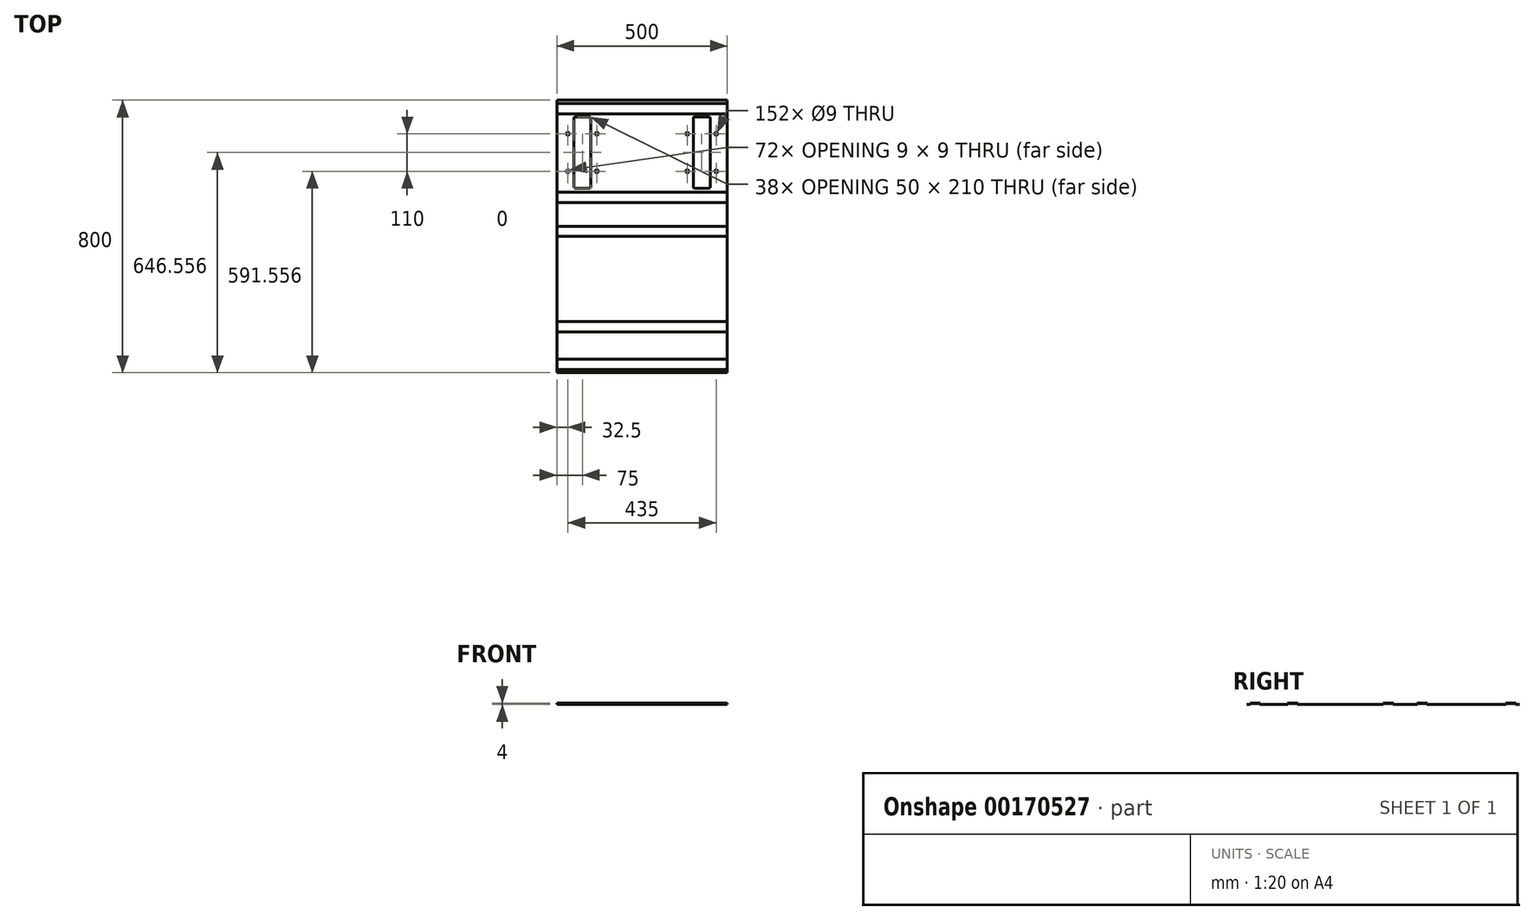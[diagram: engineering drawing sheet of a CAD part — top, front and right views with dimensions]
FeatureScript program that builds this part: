
annotation { "Feature Type Name" : "Feature", "Feature Type Description" : "" }
export const myFeature = defineFeature(function(context is Context, id is Id, definition is map)
    precondition{}
    {
        {
            var Q0;
            Q0=qCreatedBy(makeId("Right.planeOp"),FACE);
            var sketch = newSketch(context, id + "F0", { "sketchPlane" : qUnion([Q0])});
            skLineSegment(sketch, "E0.bottom", {"start": v(-25.28, 0) * mm, "end": v(-14.28, 0) * mm});
            skLineSegment(sketch, "E0.top", {"start": v(-25.28, 1) * mm, "end": v(-15.28, 1) * mm});
            skLineSegment(sketch, "E0.left", {"start": v(-25.28, 0) * mm, "end": v(-25.28, 1) * mm});
            skLineSegment(sketch, "E0.right", {"start": v(774.72, 0) * mm, "end": v(774.72, 1) * mm});
            skLineSegment(sketch, "E1.0", {"start": v(-14.28, 3) * mm, "end": v(13.72, 3) * mm});
            skLineSegment(sketch, "E2.0", {"start": v(-15.28, 4) * mm, "end": v(14.72, 4) * mm});
            skLineSegment(sketch, "E3", {"start": v(764.72, 4) * mm, "end": v(764.72, 1) * mm});
            skLineSegment(sketch, "E4", {"start": v(734.72, 4) * mm, "end": v(734.72, 1) * mm});
            skPoint(sketch, "E5.orphan", {"position": v(734.72, 10.86) * mm});
            skPoint(sketch, "E6.orphan", {"position": v(764.72, 9.78) * mm});
            skLineSegment(sketch, "E7.0", {"start": v(763.72, 3) * mm, "end": v(763.72, 1) * mm});
            skLineSegment(sketch, "E8.0", {"start": v(735.72, 3) * mm, "end": v(735.72, 1) * mm});
            skLineSegment(sketch, "E9.trimOffspring", {"start": v(764.72, 1) * mm, "end": v(774.72, 1) * mm});
            skLineSegment(sketch, "E10", {"start": v(763.72, 1) * mm, "end": v(763.72, 0) * mm});
            skLineSegment(sketch, "E11", {"start": v(735.72, 1) * mm, "end": v(735.72, 0) * mm});
            skLineSegment(sketch, "E12.trimOffspring", {"start": v(735.72, 3) * mm, "end": v(763.72, 3) * mm});
            skLineSegment(sketch, "E13.trimOffspring", {"start": v(763.72, 0) * mm, "end": v(774.72, 0) * mm});
            skLineSegment(sketch, "E14", {"start": v(504.72, 4) * mm, "end": v(504.72, 1) * mm});
            skLineSegment(sketch, "E15", {"start": v(474.72, 4) * mm, "end": v(474.72, 1) * mm});
            skLineSegment(sketch, "E16.trimOffspring", {"start": v(503.72, 0) * mm, "end": v(735.72, 0) * mm});
            skLineSegment(sketch, "E17.trimOffspring", {"start": v(504.72, 1) * mm, "end": v(734.72, 1) * mm});
            skLineSegment(sketch, "E18.trimOffspring", {"start": v(475.72, 3) * mm, "end": v(475.72, 0) * mm});
            skLineSegment(sketch, "E19.trimOffspring", {"start": v(503.72, 3) * mm, "end": v(503.72, 0) * mm});
            skLineSegment(sketch, "E20.trimOffspring", {"start": v(475.72, 3) * mm, "end": v(503.72, 3) * mm});
            skPoint(sketch, "E21.orphan", {"position": v(474.72, 0) * mm});
            skLineSegment(sketch, "E22.trimOffspring", {"start": v(734.72, 4) * mm, "end": v(764.72, 4) * mm});
            skLineSegment(sketch, "E23", {"start": v(-15.28, 4) * mm, "end": v(-15.28, 1) * mm});
            skLineSegment(sketch, "E24", {"start": v(14.72, 4) * mm, "end": v(14.72, 1) * mm});
            skLineSegment(sketch, "E25", {"start": v(94.72, 4) * mm, "end": v(94.72, 1) * mm});
            skLineSegment(sketch, "E26", {"start": v(124.72, 4) * mm, "end": v(124.72, 1) * mm});
            skPoint(sketch, "E27.orphan", {"position": v(-15.28, 10.77) * mm});
            skLineSegment(sketch, "E28.0", {"start": v(-14.28, 3) * mm, "end": v(-14.28, 0) * mm});
            skLineSegment(sketch, "E29.0", {"start": v(95.72, 4) * mm, "end": v(95.72, 0) * mm});
            skLineSegment(sketch, "E30.0", {"start": v(123.72, 3) * mm, "end": v(123.72, 0) * mm});
            skPoint(sketch, "E31.orphan", {"position": v(124.72, 12.9) * mm});
            skPoint(sketch, "E32.orphan", {"position": v(94.72, 12.13) * mm});
            skLineSegment(sketch, "E33.trimOffspring", {"start": v(14.72, 1) * mm, "end": v(94.72, 1) * mm});
            skPoint(sketch, "E34.orphan", {"position": v(-15.28, 0) * mm});
            skLineSegment(sketch, "E35.trimOffspring", {"start": v(13.72, 0) * mm, "end": v(95.72, 0) * mm});
            skLineSegment(sketch, "E36.trimOffspring", {"start": v(94.72, 3) * mm, "end": v(123.72, 3) * mm});
            skLineSegment(sketch, "E37.trimOffspring", {"start": v(13.72, 3) * mm, "end": v(13.72, 0) * mm});
            skPoint(sketch, "E38.orphan", {"position": v(14.72, 11.16) * mm});
            skLineSegment(sketch, "E39.trimOffspring", {"start": v(94.72, 4) * mm, "end": v(124.72, 4) * mm});
            skPoint(sketch, "E40.orphan", {"position": v(14.72, 0) * mm});
            skLineSegment(sketch, "E41.trimOffspring", {"start": v(124.72, 1) * mm, "end": v(374.72, 1) * mm});
            skLineSegment(sketch, "E42.trimOffspring", {"start": v(123.72, 0) * mm, "end": v(375.72, 0) * mm});
            skPoint(sketch, "E43.orphan", {"position": v(94.72, 0) * mm});
            skPoint(sketch, "E44.orphan", {"position": v(124.72, 0) * mm});
            skLineSegment(sketch, "E45.trimOffspring", {"start": v(375.72, 3) * mm, "end": v(404.01, 3) * mm});
            skLineSegment(sketch, "E46", {"start": v(374.72, 4) * mm, "end": v(374.72, 1) * mm});
            skLineSegment(sketch, "E47", {"start": v(405, 4) * mm, "end": v(405.03, 1) * mm});
            skLineSegment(sketch, "E48.trimOffspring", {"start": v(374.72, 4) * mm, "end": v(405, 4) * mm});
            skLineSegment(sketch, "E49.trimOffspring", {"start": v(474.72, 4) * mm, "end": v(504.72, 4) * mm});
            skLineSegment(sketch, "E50.0", {"start": v(404.01, 3) * mm, "end": v(404.05, -0.01) * mm});
            skLineSegment(sketch, "E51.trimOffspring", {"start": v(405.03, 1) * mm, "end": v(474.72, 1) * mm});
            skLineSegment(sketch, "E52.trimOffspring", {"start": v(404.05, 0) * mm, "end": v(475.72, 0) * mm});
            skLineSegment(sketch, "E53.trimOffspring", {"start": v(375.72, 3) * mm, "end": v(375.72, 0) * mm});
            skPoint(sketch, "E54.orphan", {"position": v(374.72, 0) * mm});
            skPoint(sketch, "E55.orphan", {"position": v(374.72, 30.11) * mm});
            skPoint(sketch, "E56.orphan", {"position": v(404.72, 31.49) * mm});
            skSolve(sketch);
        }
        {
            var Q0;
            {var subQ3=sQuery(id+"F0.wireOp",EDGE,"E2.0");Q0=makeQuery(id+"F0.imprint","IMPRINT",FACE,{"disambiguationData":[TD([[makeQuery(id+"F0.imprint","IMPRINT",EDGE,{"derivedFrom":subQ3}),-1.0]])]});}
            var Q1;
            Q1=makeQuery(id+"F0.imprint","IMPRINT",FACE,{"disambiguationData":[TD([[makeQuery(id+"F0.imprint","IMPRINT",EDGE,{"derivedFrom":sQuery(id+"F0.wireOp",EDGE,"E0.right")}),1.0]])]});
            var Q2;
            {var subQ0=sQuery(id+"F0.wireOp",EDGE,"E35.trimOffspring");Q2=makeQuery(id+"F0.imprint","IMPRINT",FACE,{"disambiguationData":[TD([[makeQuery(id+"F0.imprint","IMPRINT",EDGE,{"derivedFrom":subQ0}),1.0]])]});}
            var Q3;
            {var subQ0=sQuery(id+"F0.wireOp",EDGE,"E37.trimOffspring");var subQ1=sQuery(id+"F0.wireOp",EDGE,"E1.0");var subQ2=makeQuery(id+"F0.imprint","INTERSECT",VERTEX,{"derivedFrom":[subQ1,subQ0]});Q3=makeQuery(id+"F0.imprint","IMPRINT",FACE,{"disambiguationData":[TD([[makeQuery(id+"F0.imprint","IMPRINT",EDGE,{"disambiguationData":[TD([[subQ2,1.0]])],"derivedFrom":subQ1}),-1.0]])]});}
            var Q4;
            {var subQ0=sQuery(id+"F0.wireOp",EDGE,"E39.trimOffspring");var subQ1=sQuery(id+"F0.wireOp",EDGE,"E25");var subQ2=makeQuery(id+"F0.imprint","INTERSECT",VERTEX,{"derivedFrom":[subQ1,subQ0]});Q4=makeQuery(id+"F0.imprint","IMPRINT",FACE,{"disambiguationData":[TD([[makeQuery(id+"F0.imprint","IMPRINT",EDGE,{"disambiguationData":[TD([[subQ2,-1.0]])],"derivedFrom":subQ1}),1.0]])]});}
            var Q5;
            Q5=makeQuery(id+"F0.imprint","IMPRINT",FACE,{"disambiguationData":[TD([[makeQuery(id+"F0.imprint","IMPRINT",EDGE,{"derivedFrom":sQuery(id+"F0.wireOp",EDGE,"E0.bottom")}),1.0]])]});
            extrude(context, id + "F1", {"entities" : qUnion([Q0, Q1, Q2, Q3, Q4, Q5]), "oppositeDirection" : true, "depth" : 500 * mm});
        }
        {
            var Q0;
            Q0=makeQuery(id+"F1.opExtrude","SWEPT_FACE",FACE,{"disambiguationData":[OSD([sQuery(id+"F0.wireOp",EDGE,"E17.trimOffspring")])]});
            var sketch = newSketch(context, id + "F2", { "sketchPlane" : qUnion([Q0])});
            skLineSegment(sketch, "E57", {"start": v(-250, 774.7) * mm, "end": v(-250, 270.25) * mm, "construction": true});
            skLineSegment(sketch, "E58", {"start": v(0.24, 551.28) * mm, "end": v(-799.76, 551.28) * mm, "construction": true});
            skLineSegment(sketch, "E59.bottom", {"start": v(-445, 726.28) * mm, "end": v(-405, 726.28) * mm});
            skLineSegment(sketch, "E59.top", {"start": v(-445, 516.28) * mm, "end": v(-405, 516.28) * mm});
            skLineSegment(sketch, "E59.left", {"start": v(-450, 721.28) * mm, "end": v(-450, 521.28) * mm});
            skLineSegment(sketch, "E59.right", {"start": v(-400, 721.28) * mm, "end": v(-400, 521.28) * mm});
            skCircle(sketch, "E60", {"center": v(-467.5, 676.28) * mm, "radius": 4.5 * mm});
            skLineSegment(sketch, "E61", {"start": v(-450, 621.28) * mm, "end": v(-872.27, 621.28) * mm, "construction": true});
            skLineSegment(sketch, "E62", {"start": v(-425, 726.28) * mm, "end": v(-425, 666.8) * mm, "construction": true});
            skCircle(sketch, "E63.MirrorC", {"center": v(-467.5, 566.28) * mm, "radius": 4.5 * mm});
            skCircle(sketch, "E64.MirrorC", {"center": v(-382.5, 676.28) * mm, "radius": 4.5 * mm});
            skCircle(sketch, "E65.MirrorC", {"center": v(-382.5, 566.28) * mm, "radius": 4.5 * mm});
            skPoint(sketch, "E66.visualSharp", {"position": v(-450, 726.28) * mm});
            skArc(sketch, "E66.filletArc", {"start": v(-445, 726.28) * mm, "mid": v(-448.54, 724.81) * mm, "end": v(-450, 721.28) * mm});
            skPoint(sketch, "E67.visualSharp", {"position": v(-400, 726.28) * mm});
            skArc(sketch, "E67.filletArc", {"start": v(-400, 721.28) * mm, "mid": v(-401.46, 724.81) * mm, "end": v(-405, 726.28) * mm});
            skPoint(sketch, "E68.visualSharp", {"position": v(-450, 516.28) * mm});
            skArc(sketch, "E68.filletArc", {"start": v(-450, 521.28) * mm, "mid": v(-448.54, 517.74) * mm, "end": v(-445, 516.28) * mm});
            skPoint(sketch, "E69.visualSharp", {"position": v(-400, 516.28) * mm});
            skArc(sketch, "E69.filletArc", {"start": v(-405, 516.28) * mm, "mid": v(-401.46, 517.74) * mm, "end": v(-400, 521.28) * mm});
            skArc(sketch, "E70.MirrorCS", {"start": v(-95, 516.28) * mm, "mid": v(-98.54, 517.74) * mm, "end": v(-100, 521.28) * mm});
            skArc(sketch, "E71.MirrorCS", {"start": v(-100, 721.28) * mm, "mid": v(-98.54, 724.81) * mm, "end": v(-95, 726.28) * mm});
            skArc(sketch, "E72.MirrorCS", {"start": v(-50, 521.28) * mm, "mid": v(-51.46, 517.74) * mm, "end": v(-55, 516.28) * mm});
            skArc(sketch, "E73.MirrorCS", {"start": v(-55, 726.28) * mm, "mid": v(-51.46, 724.81) * mm, "end": v(-50, 721.28) * mm});
            skCircle(sketch, "E74.MirrorC", {"center": v(-32.5, 566.28) * mm, "radius": 4.5 * mm});
            skCircle(sketch, "E75.MirrorC", {"center": v(-117.5, 676.28) * mm, "radius": 4.5 * mm});
            skCircle(sketch, "E76.MirrorC", {"center": v(-117.5, 566.28) * mm, "radius": 4.5 * mm});
            skCircle(sketch, "E77.MirrorC", {"center": v(-32.5, 676.28) * mm, "radius": 4.5 * mm});
            skPoint(sketch, "E78.MirrorP", {"position": v(-50, 516.28) * mm});
            skLineSegment(sketch, "E79.MirrorCS", {"start": v(-55, 726.28) * mm, "end": v(-95, 726.28) * mm});
            skLineSegment(sketch, "E80.MirrorCS", {"start": v(-55, 516.28) * mm, "end": v(-95, 516.28) * mm});
            skPoint(sketch, "E81.MirrorP", {"position": v(-100, 516.28) * mm});
            skPoint(sketch, "E82.MirrorP", {"position": v(-100, 726.28) * mm});
            skLineSegment(sketch, "E83.MirrorCS", {"start": v(-50, 721.28) * mm, "end": v(-50, 521.28) * mm});
            skLineSegment(sketch, "E84.MirrorCS", {"start": v(-100, 721.28) * mm, "end": v(-100, 521.28) * mm});
            skPoint(sketch, "E85.MirrorP", {"position": v(-50, 726.28) * mm});
            skLineSegment(sketch, "E86", {"start": v(-250, 734.72) * mm, "end": v(-250, 839.36) * mm, "construction": true});
            skSolve(sketch);
        }
        {
            var Q0;
            Q0 = qSketchRegion(id + "F2", true);
            extrude(context, id + "F3", {"entities" : qUnion([Q0]), "operationType" : NewBodyOperationType.REMOVE, "endBound" : BoundingType.THROUGH_ALL, "oppositeDirection" : true, "depth" : 25 * mm});
        }
    });
